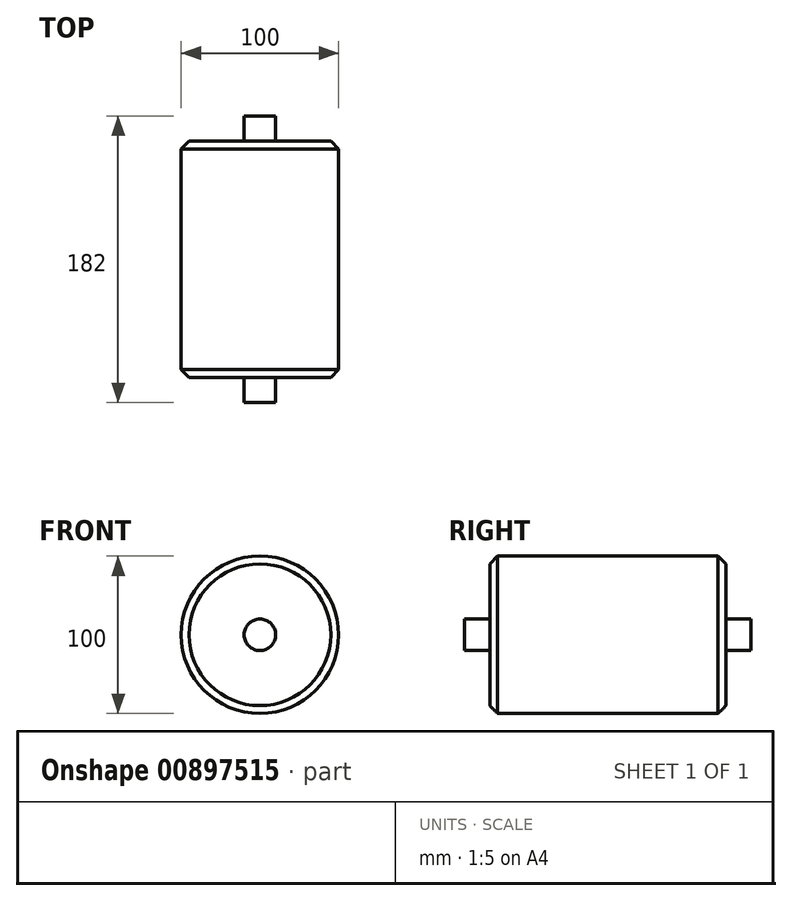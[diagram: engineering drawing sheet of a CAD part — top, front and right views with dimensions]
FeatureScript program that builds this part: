
annotation { "Feature Type Name" : "Feature", "Feature Type Description" : "" }
export const myFeature = defineFeature(function(context is Context, id is Id, definition is map)
    precondition{}
    {
        {
            var Q0;
            Q0=qCreatedBy(makeId("Front.planeOp"),FACE);
            var sketch = newSketch(context, id + "F0", { "sketchPlane" : qUnion([Q0])});
            skCircle(sketch, "E0", {"center": v(0, 0) * mm, "radius": 50 * mm});
            skSolve(sketch);
        }
        {
            var Q0;
            Q0=makeQuery(id+"F0.imprint","IMPRINT",FACE,{"disambiguationData":[TD([[makeQuery(id+"F0.imprint","IMPRINT",EDGE,{"derivedFrom":sQuery(id+"F0.wireOp",EDGE,"E0")}),1.0]])]});
            extrude(context, id + "F1", {"entities" : qUnion([Q0]), "depth" : 150 * mm, "offsetDistance" : 25.4 * mm});
        }
        {
            var Q0;
            Q0=makeQuery(id+"F1.opExtrude","CAP_FACE",FACE,{"disambiguationData":[OSD([sQuery(id+"F0.wireOp",EDGE,"E0")])],"isStart":false});
            var sketch = newSketch(context, id + "F2", { "sketchPlane" : qUnion([Q0])});
            skCircle(sketch, "E1", {"center": v(0, 0) * mm, "radius": 10 * mm});
            skSolve(sketch);
        }
        {
            var Q0;
            Q0 = qSketchRegion(id + "F2", true);
            extrude(context, id + "F3", {"entities" : qUnion([Q0]), "operationType" : NewBodyOperationType.ADD, "depth" : 16 * mm, "offsetDistance" : 25.4 * mm});
        }
        {
            var Q0;
            Q0=makeQuery(id+"F1.opExtrude","CAP_FACE",FACE,{"disambiguationData":[OSD([sQuery(id+"F0.wireOp",EDGE,"E0")])],"isStart":true});
            var sketch = newSketch(context, id + "F4", { "sketchPlane" : qUnion([Q0])});
            skCircle(sketch, "E2", {"center": v(0, 0) * mm, "radius": 10 * mm});
            skSolve(sketch);
        }
        {
            var Q0;
            Q0=makeQuery(id+"F4.imprint","IMPRINT",FACE,{"disambiguationData":[TD([[makeQuery(id+"F4.imprint","IMPRINT",EDGE,{"derivedFrom":sQuery(id+"F4.wireOp",EDGE,"E2")}),1.0]])]});
            extrude(context, id + "F5", {"entities" : qUnion([Q0]), "operationType" : NewBodyOperationType.ADD, "depth" : 16 * mm, "offsetDistance" : 25.4 * mm});
        }
        {
            var Q0;
            Q0=makeQuery(id+"F1.opExtrude","CAP_EDGE",EDGE,{"disambiguationData":[OSD([sQuery(id+"F0.wireOp",EDGE,"E0")])],"isStart":true});
            var Q1;
            Q1=makeQuery(id+"F1.opExtrude","CAP_EDGE",EDGE,{"disambiguationData":[OSD([sQuery(id+"F0.wireOp",EDGE,"E0")])],"isStart":false});
            chamfer(context, id + "F6", {"entities" : qUnion([Q0, Q1]), "width" : 5 * mm, "tangentPropagation" : true});
        }
    });
